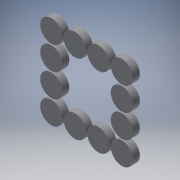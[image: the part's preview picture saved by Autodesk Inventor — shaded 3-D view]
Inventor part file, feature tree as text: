
AUTODESK INVENTOR PART (.ipt)
format: ipt  version: 2019.3 (Build 233278000, 278)  size: 289,280 bytes
history: native  units: mm
features: sketch x8, extrude x5, reference x4, plane x2, other x2, sweep x1
ambient origin geometry x8: Origin, YZ Plane, XZ Plane, XY Plane, X Axis, Y Axis, Z Axis, Center Point
bodies: Solid1 (feature_tree)
feature tree (22):
  extrude  "Extrusion1"  Depth=15.0mm TaperAngle=0.0deg
  plane  "Work Plane1"
  extrude  "Extrusion2"  Depth=1.0mm
  sketch  "Sketch3"  dims[d6=1.0mm d7=1.0mm]
  sketch  "Sketch4"  dims[d9=2.0mm d10=6.0mm]
  plane  "Work Plane2"
  sweep  "Sweep1"
  extrude  "Extrusion3"  Depth=6.0mm
  extrude  "Extrusion4"  Depth=4.0mm
  extrude  "Extrusion5"  TaperAngle=135.0deg  [1 undecoded]
  sketch  "Sketch1"  dims[d0=5.0mm d1=0.0mm d2=15.0mm d3=0.0mm]
  reference  "Reference1"
  sketch  "Sketch2"  dims[d4=1.0mm d5=1.0mm]
  reference  "Reference2"
  reference  "Reference3"
  reference  "Reference4"
  sketch  "Sketch5"  dims[d11=6.0mm d12=4.0mm]
  sketch  "Sketch6"  dims[d13=40.0mm d15=17.0mm d16=40.0mm d18=17.0mm d21=135.0deg]
  sketch  "Sketch7"  dims[d23=5.0mm]
  sketch  "Sketch8"  dims[d24=0.0mm d25=0.0mm d26=7.5mm d27=13.5mm d28=34.5mm d29=12.0mm d30=0.0mm d31=8.0mm d32=12.0mm d33=0.0mm d34=1.1mm d35=1.1mm d36=1.1mm d37=1.1mm d38=5.2mm d39=0.0mm]
  other  "Assembly1"
  other  "WeightHolder:1"
note: 1 required parameter value undecoded (feature->parameter linkage not recoverable at this tier; creation-order binding heuristic only, values carry confidence <= 0.55)
